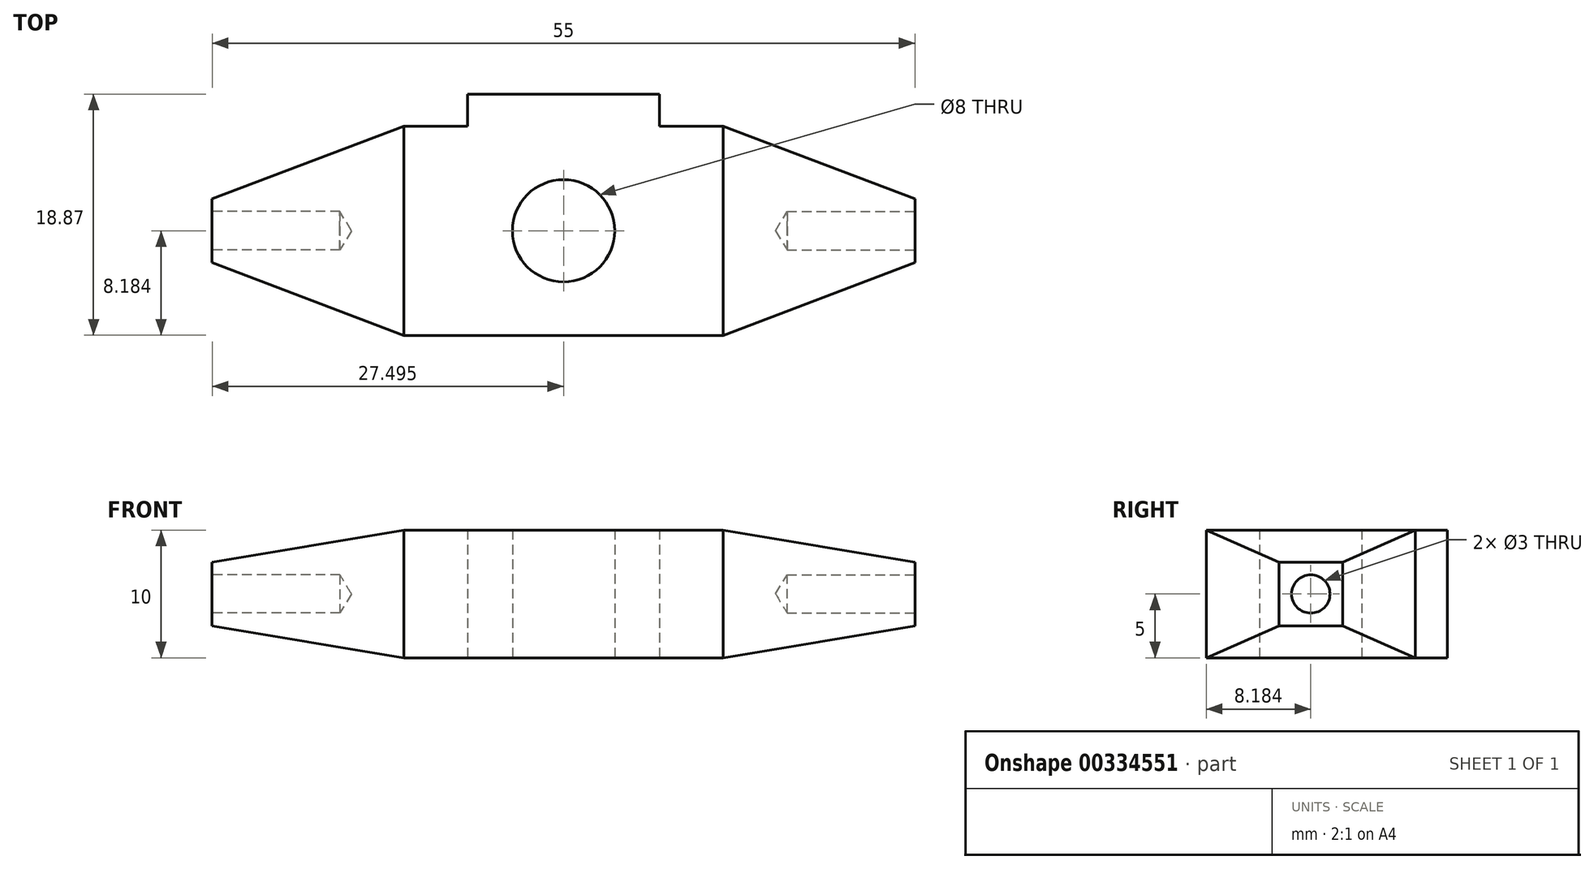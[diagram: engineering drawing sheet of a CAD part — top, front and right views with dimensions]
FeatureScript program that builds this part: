
annotation { "Feature Type Name" : "Feature", "Feature Type Description" : "" }
export const myFeature = defineFeature(function(context is Context, id is Id, definition is map)
    precondition{}
    {
        {
            var Q0;
            Q0=qCreatedBy(makeId("Top.planeOp"),FACE);
            var sketch = newSketch(context, id + "F0", { "sketchPlane" : qUnion([Q0])});
            skLineSegment(sketch, "E0.top", {"start": v(39.24, 15) * mm, "end": v(24.24, 15) * mm});
            skLineSegment(sketch, "E0.left", {"start": v(39.24, -2.5) * mm, "end": v(39.24, 15) * mm});
            skLineSegment(sketch, "E0.right", {"start": v(24.24, -2.5) * mm, "end": v(24.24, 15) * mm});
            skPoint(sketch, "E0.middle", {"position": v(0, 0) * mm});
            skLineSegment(sketch, "E1.bottom", {"start": v(24.24, 15) * mm, "end": v(39.24, 15) * mm});
            skLineSegment(sketch, "E1.top", {"start": v(24.24, 0) * mm, "end": v(39.24, 0) * mm});
            skLineSegment(sketch, "E1.left", {"start": v(24.24, 15) * mm, "end": v(24.24, 0) * mm});
            skLineSegment(sketch, "E1.right", {"start": v(39.24, 15) * mm, "end": v(39.24, 0) * mm});
            skCircle(sketch, "E2", {"center": v(31.74, 7.5) * mm, "radius": 4 * mm});
            skPoint(sketch, "E2.centerSnap0", {"position": v(39.24, 7.5) * mm});
            skPoint(sketch, "E2.centerSnap1", {"position": v(31.74, 15) * mm});
            skLineSegment(sketch, "E3.top", {"start": v(24.24, -2.5) * mm, "end": v(39.24, -2.5) * mm});
            skLineSegment(sketch, "E3.left", {"start": v(24.24, 0) * mm, "end": v(24.24, -2.5) * mm});
            skLineSegment(sketch, "E3.right", {"start": v(39.24, 0) * mm, "end": v(39.24, -2.5) * mm});
            skLineSegment(sketch, "E4.bottom", {"start": v(31.74, -2.5) * mm, "end": v(59.24, -2.5) * mm});
            skLineSegment(sketch, "E4.top", {"start": v(15.87, -18.87) * mm, "end": v(59.24, -18.87) * mm});
            skLineSegment(sketch, "E4.right", {"start": v(59.24, -2.5) * mm, "end": v(59.24, -18.87) * mm});
            skLineSegment(sketch, "E5.bottom", {"start": v(31.74, -2.5) * mm, "end": v(4.24, -2.5) * mm});
            skLineSegment(sketch, "E5.top", {"start": v(15.87, -18.87) * mm, "end": v(4.24, -18.87) * mm});
            skLineSegment(sketch, "E5.right", {"start": v(4.24, -2.5) * mm, "end": v(4.24, -18.87) * mm});
            skCircle(sketch, "E6", {"center": v(31.74, -10.69) * mm, "radius": 4 * mm});
            skPoint(sketch, "E6.centerSnap0", {"position": v(4.24, -10.69) * mm});
            skSolve(sketch);
        }
        {
            var Q0;
            Q0=makeQuery(id+"F0.imprint","IMPRINT",FACE,{"disambiguationData":[TD([[makeQuery(id+"F0.imprint","IMPRINT",EDGE,{"derivedFrom":sQuery(id+"F0.wireOp",EDGE,"E4.top")}),1.0]])]});
            var Q1;
            Q1=makeQuery(id+"F0.imprint","IMPRINT",FACE,{"disambiguationData":[TD([[makeQuery(id+"F0.imprint","IMPRINT",EDGE,{"derivedFrom":sQuery(id+"F0.wireOp",EDGE,"E1.top")}),-1.0]])]});
            var Q2;
            Q2=makeQuery(id+"F0.imprint","IMPRINT",FACE,{"disambiguationData":[TD([[makeQuery(id+"F0.imprint","IMPRINT",EDGE,{"derivedFrom":sQuery(id+"F0.wireOp",EDGE,"E1.bottom")}),-1.0]])]});
            extrude(context, id + "F1", {"entities" : qUnion([Q0, Q1, Q2]), "depth" : 10 * mm});
        }
        {
            var Q0;
            Q0=makeQuery(id+"F1.opExtrude","CAP_FACE",FACE,{"disambiguationData":[OSD([sQuery(id+"F0.wireOp",EDGE,"E1.bottom"),sQuery(id+"F0.wireOp",EDGE,"E1.left"),sQuery(id+"F0.wireOp",EDGE,"E1.right"),sQuery(id+"F0.wireOp",EDGE,"E2"),sQuery(id+"F0.wireOp",EDGE,"E3.left"),sQuery(id+"F0.wireOp",EDGE,"E3.right"),sQuery(id+"F0.wireOp",EDGE,"E4.bottom"),sQuery(id+"F0.wireOp",EDGE,"E4.top"),sQuery(id+"F0.wireOp",EDGE,"E4.right"),sQuery(id+"F0.wireOp",EDGE,"E5.bottom"),sQuery(id+"F0.wireOp",EDGE,"E5.top"),sQuery(id+"F0.wireOp",EDGE,"E5.right"),sQuery(id+"F0.wireOp",EDGE,"E6")])],"isStart":false});
            var sketch = newSketch(context, id + "F2", { "sketchPlane" : qUnion([Q0])});
            skLineSegment(sketch, "E7", {"start": v(59.24, -10.69) * mm, "end": v(59.24, -8.19) * mm});
            skLineSegment(sketch, "E8", {"start": v(59.24, -8.19) * mm, "end": v(59.24, -13.19) * mm});
            skLineSegment(sketch, "E9", {"start": v(59.24, -18.87) * mm, "end": v(44.24, -18.87) * mm});
            skLineSegment(sketch, "E10", {"start": v(44.24, -18.87) * mm, "end": v(44.24, -2.5) * mm});
            skLineSegment(sketch, "E11", {"start": v(44.24, -2.5) * mm, "end": v(59.24, -8.19) * mm});
            skLineSegment(sketch, "E12", {"start": v(59.24, -13.19) * mm, "end": v(44.24, -18.87) * mm});
            skSolve(sketch);
        }
        {
            var Q0;
            {var subQ0=sQuery(id+"F2.wireOp",EDGE,"E11");Q0=makeQuery(id+"F2.imprint","IMPRINT",FACE,{"disambiguationData":[TD([[makeQuery(id+"F2.imprint","IMPRINT",EDGE,{"derivedFrom":subQ0}),1.0]])]});}
            var Q1;
            {var subQ0=sQuery(id+"F2.wireOp",EDGE,"E9");Q1=makeQuery(id+"F2.imprint","IMPRINT",FACE,{"disambiguationData":[TD([[makeQuery(id+"F2.imprint","IMPRINT",EDGE,{"derivedFrom":subQ0}),-1.0]])]});}
            extrude(context, id + "F3", {"entities" : qUnion([Q0, Q1]), "operationType" : NewBodyOperationType.REMOVE, "oppositeDirection" : true, "depth" : 25 * mm});
        }
        {
            var Q0;
            Q0=makeQuery(id+"F1.opExtrude","CAP_FACE",FACE,{"disambiguationData":[OSD([sQuery(id+"F0.wireOp",EDGE,"E1.bottom"),sQuery(id+"F0.wireOp",EDGE,"E1.left"),sQuery(id+"F0.wireOp",EDGE,"E1.right"),sQuery(id+"F0.wireOp",EDGE,"E2"),sQuery(id+"F0.wireOp",EDGE,"E3.left"),sQuery(id+"F0.wireOp",EDGE,"E3.right"),sQuery(id+"F0.wireOp",EDGE,"E4.bottom"),sQuery(id+"F0.wireOp",EDGE,"E4.top"),sQuery(id+"F0.wireOp",EDGE,"E4.right"),sQuery(id+"F0.wireOp",EDGE,"E5.bottom"),sQuery(id+"F0.wireOp",EDGE,"E5.top"),sQuery(id+"F0.wireOp",EDGE,"E5.right"),sQuery(id+"F0.wireOp",EDGE,"E6")])],"isStart":false});
            var sketch = newSketch(context, id + "F4", { "sketchPlane" : qUnion([Q0])});
            skLineSegment(sketch, "E13", {"start": v(4.24, -2.5) * mm, "end": v(19.24, -2.5) * mm});
            skLineSegment(sketch, "E14", {"start": v(19.24, -2.5) * mm, "end": v(19.24, -18.87) * mm});
            skLineSegment(sketch, "E15", {"start": v(4.24, -10.69) * mm, "end": v(4.24, -8.19) * mm});
            skLineSegment(sketch, "E16", {"start": v(4.24, -8.19) * mm, "end": v(4.24, -13.19) * mm});
            skLineSegment(sketch, "E17", {"start": v(4.24, -13.19) * mm, "end": v(19.24, -18.87) * mm});
            skLineSegment(sketch, "E18", {"start": v(4.24, -8.19) * mm, "end": v(19.24, -2.5) * mm});
            skSolve(sketch);
        }
        {
            var Q0;
            {var subQ0=sQuery(id+"F4.wireOp",EDGE,"E13");Q0=makeQuery(id+"F4.imprint","IMPRINT",FACE,{"disambiguationData":[TD([[makeQuery(id+"F4.imprint","IMPRINT",EDGE,{"derivedFrom":subQ0}),1.0]])]});}
            var Q1;
            {var subQ0=sQuery(id+"F4.wireOp",EDGE,"E17");Q1=makeQuery(id+"F4.imprint","IMPRINT",FACE,{"disambiguationData":[TD([[makeQuery(id+"F4.imprint","IMPRINT",EDGE,{"derivedFrom":subQ0}),-1.0]])]});}
            extrude(context, id + "F5", {"entities" : qUnion([Q0, Q1]), "operationType" : NewBodyOperationType.REMOVE, "oppositeDirection" : true, "depth" : 25 * mm});
        }
        {
            var Q0;
            Q0=makeQuery(id+"F1.opExtrude","CAP_EDGE",EDGE,{"disambiguationData":[OSD([sQuery(id+"F0.wireOp",EDGE,"E5.right")])],"isStart":false});
            var Q1;
            Q1=makeQuery(id+"F1.opExtrude","CAP_EDGE",EDGE,{"disambiguationData":[OSD([sQuery(id+"F0.wireOp",EDGE,"E5.right")])],"isStart":true});
            var Q2;
            Q2=makeQuery(id+"F1.opExtrude","CAP_EDGE",EDGE,{"disambiguationData":[OSD([sQuery(id+"F0.wireOp",EDGE,"E4.right")])],"isStart":false});
            var Q3;
            Q3=makeQuery(id+"F1.opExtrude","CAP_EDGE",EDGE,{"disambiguationData":[OSD([sQuery(id+"F0.wireOp",EDGE,"E4.right")])],"isStart":true});
            chamfer(context, id + "F6", {"entities" : qUnion([Q0, Q1, Q2, Q3]), "chamferType" : ChamferType.TWO_OFFSETS, "width1" : 15 * mm, "oppositeDirection" : false, "width2" : 2.5 * mm, "tangentPropagation" : true});
        }
        {
            var Q0;
            Q0=makeQuery(id+"F1.opExtrude","SWEPT_FACE",FACE,{"disambiguationData":[OSD([sQuery(id+"F0.wireOp",EDGE,"E5.right")])]});
            var sketch = newSketch(context, id + "F7", { "sketchPlane" : qUnion([Q0])});
            skCircle(sketch, "E19", {"center": v(10.69, 5) * mm, "radius": 1.5 * mm});
            skPoint(sketch, "E19.centerSnap0", {"position": v(10.69, 7.5) * mm});
            skPoint(sketch, "E19.centerSnap1", {"position": v(8.19, 5) * mm});
            skSolve(sketch);
        }
        {
            var Q0;
            Q0=makeQuery(id+"F1.opExtrude","SWEPT_FACE",FACE,{"disambiguationData":[OSD([sQuery(id+"F0.wireOp",EDGE,"E4.right")])]});
            var sketch = newSketch(context, id + "F8", { "sketchPlane" : qUnion([Q0])});
            skCircle(sketch, "E20", {"center": v(-10.69, 5) * mm, "radius": 1.5 * mm});
            skPoint(sketch, "E20.centerSnap0", {"position": v(-8.19, 5) * mm});
            skPoint(sketch, "E20.centerSnap1", {"position": v(-10.69, 7.5) * mm});
            skSolve(sketch);
        }
        {
            var Q0;
            Q0=sQuery(id+"F8.wireOp",VERTEX,"E20.center");
            var Q1;
            Q1=sQuery(id+"F7.wireOp",VERTEX,"E19.center");
            var Q2;
            Q2=makeQuery(id+"F1.opExtrude","SWEPT_BODY",BODY,{"disambiguationData":[OSD([sQuery(id+"F0.wireOp",EDGE,"E1.bottom"),sQuery(id+"F0.wireOp",EDGE,"E1.left"),sQuery(id+"F0.wireOp",EDGE,"E1.right"),sQuery(id+"F0.wireOp",EDGE,"E2"),sQuery(id+"F0.wireOp",EDGE,"E3.left"),sQuery(id+"F0.wireOp",EDGE,"E3.right"),sQuery(id+"F0.wireOp",EDGE,"E4.bottom"),sQuery(id+"F0.wireOp",EDGE,"E4.top"),sQuery(id+"F0.wireOp",EDGE,"E4.right"),sQuery(id+"F0.wireOp",EDGE,"E5.bottom"),sQuery(id+"F0.wireOp",EDGE,"E5.top"),sQuery(id+"F0.wireOp",EDGE,"E5.right"),sQuery(id+"F0.wireOp",EDGE,"E6")])]});
            hole(context, id + "F9", {"style" : HoleStyle.SIMPLE, "endStyle" : HoleEndStyle.BLIND, "holeDiameter" : 3 * mm, "holeDepth" : 10 * mm, "tappedDepth" : 12 * mm, "tapClearance" : 3, "locations" : qUnion([Q0, Q1]), "scope" : qUnion([Q2])});
        }
    });
